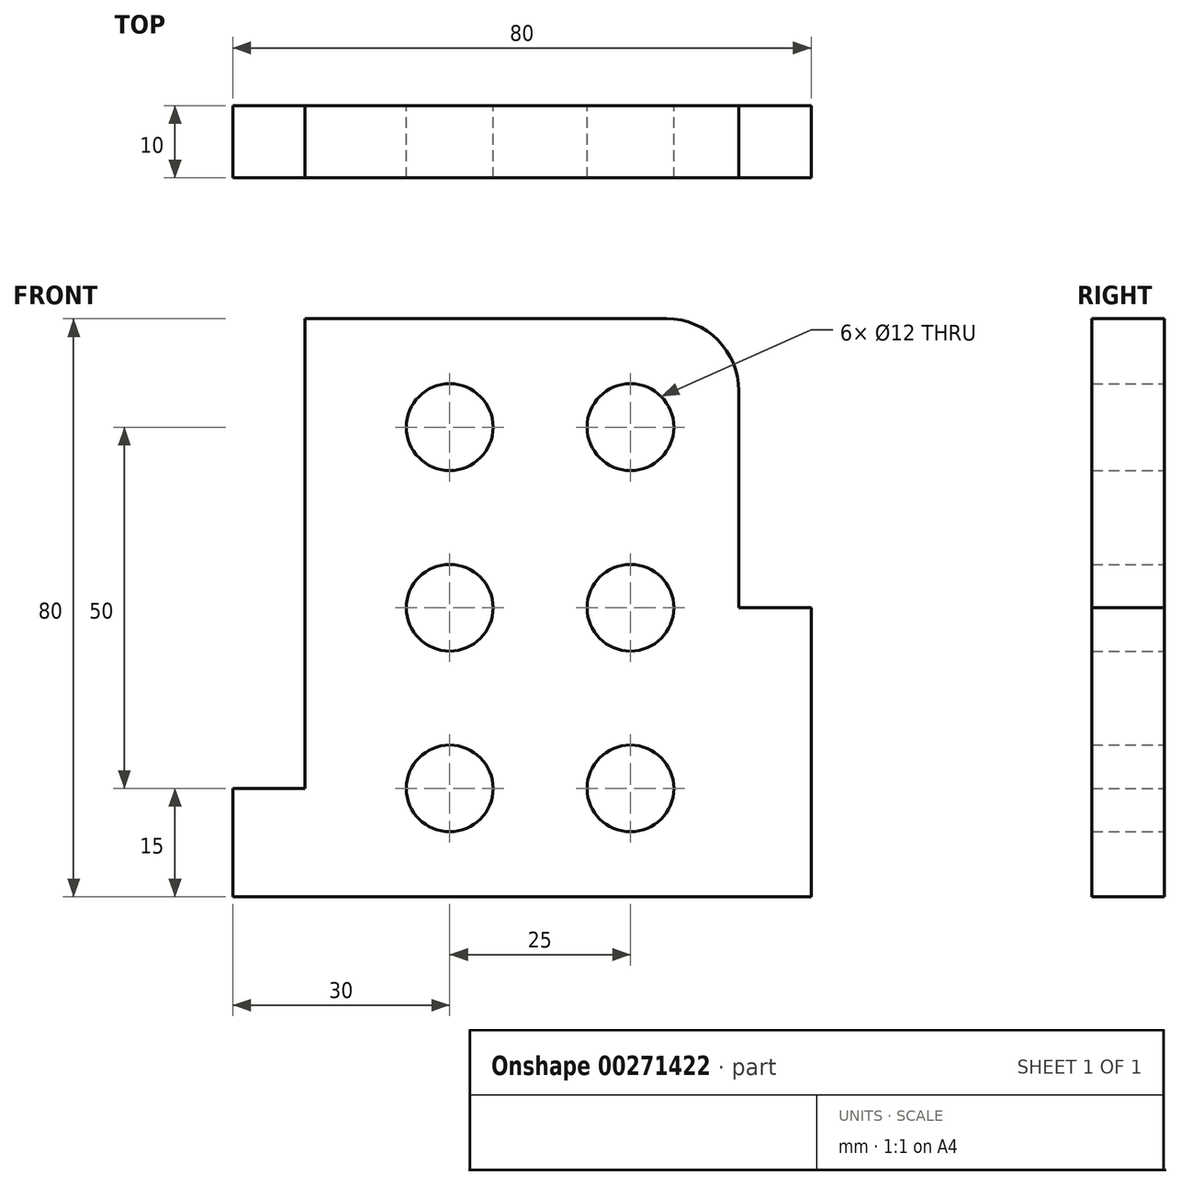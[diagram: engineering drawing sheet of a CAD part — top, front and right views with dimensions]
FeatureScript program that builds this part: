
annotation { "Feature Type Name" : "Feature", "Feature Type Description" : "" }
export const myFeature = defineFeature(function(context is Context, id is Id, definition is map)
    precondition{}
    {
        {
            var Q0;
            Q0=qCreatedBy(makeId("Front.planeOp"),FACE);
            var sketch = newSketch(context, id + "F0", { "sketchPlane" : qUnion([Q0])});
            skLineSegment(sketch, "E0", {"start": v(0, 0) * mm, "end": v(80, 0) * mm});
            skLineSegment(sketch, "E1", {"start": v(0, 0) * mm, "end": v(0, 15) * mm});
            skLineSegment(sketch, "E2", {"start": v(0, 15) * mm, "end": v(10, 15) * mm});
            skLineSegment(sketch, "E3", {"start": v(10, 15) * mm, "end": v(10, 80) * mm});
            skLineSegment(sketch, "E4", {"start": v(10, 80) * mm, "end": v(60, 80) * mm});
            skLineSegment(sketch, "E5", {"start": v(80, 0) * mm, "end": v(80, 40) * mm});
            skLineSegment(sketch, "E6", {"start": v(80, 40) * mm, "end": v(70, 40) * mm});
            skLineSegment(sketch, "E7", {"start": v(70, 40) * mm, "end": v(70, 70) * mm});
            skCircle(sketch, "E8", {"center": v(55, 65) * mm, "radius": 6 * mm});
            skCircle(sketch, "E9", {"center": v(30, 65) * mm, "radius": 6 * mm});
            skCircle(sketch, "E10", {"center": v(30, 40) * mm, "radius": 6 * mm});
            skCircle(sketch, "E11", {"center": v(55, 40) * mm, "radius": 6 * mm});
            skCircle(sketch, "E12", {"center": v(30, 15) * mm, "radius": 6 * mm});
            skCircle(sketch, "E13", {"center": v(55, 15) * mm, "radius": 6 * mm});
            skArc(sketch, "E14.filletArc", {"start": v(70, 70) * mm, "mid": v(67.07, 77.07) * mm, "end": v(60, 80) * mm});
            skSolve(sketch);
        }
        {
            var Q0;
            Q0=makeQuery(id+"F0.imprint","IMPRINT",FACE,{"disambiguationData":[TD([[makeQuery(id+"F0.imprint","IMPRINT",EDGE,{"derivedFrom":sQuery(id+"F0.wireOp",EDGE,"E0")}),1.0]])]});
            extrude(context, id + "F1", {"entities" : qUnion([Q0]), "depth" : 10 * mm});
        }
    });
